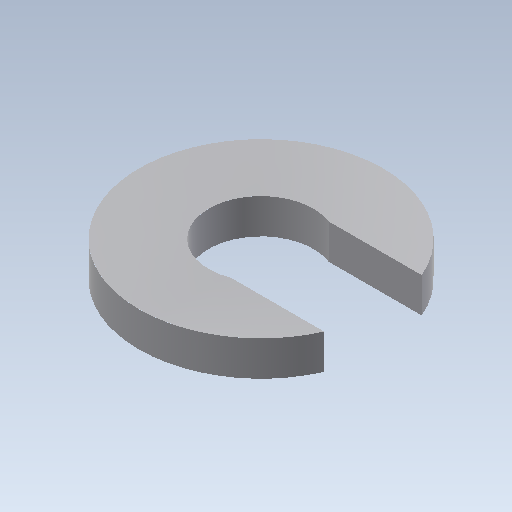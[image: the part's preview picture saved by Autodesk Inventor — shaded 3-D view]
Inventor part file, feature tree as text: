
AUTODESK INVENTOR PART (.ipt)
format: ipt  version: 2020 (Build 240168000, 168)  size: 97,792 bytes
history: native  units: mm
features: extrude x2, sketch x2
ambient origin geometry x8: Origin, YZ Plane, XZ Plane, XY Plane, X Axis, Y Axis, Z Axis, Center Point
bodies: Solid1 (feature_tree)
feature tree (4):
  extrude  "Extrusion1"  Depth=2.8mm
  extrude  "Extrusion2"  Depth=3.0mm TaperAngle=0.0deg
  sketch  "Sketch1"  dims[d0=7.0mm d1=2.8mm]
  sketch  "Sketch2"  dims[d2=1.5mm d3=3.0mm d4=0.0mm d5=2.0mm d6=0.0mm]
